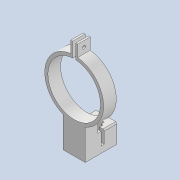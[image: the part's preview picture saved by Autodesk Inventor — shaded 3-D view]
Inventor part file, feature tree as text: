
AUTODESK INVENTOR PART (.ipt)
format: ipt  version: 2020 (Build 240168000, 168)  size: 200,704 bytes
history: native  units: mm
features: sketch x6, extrude x5, hole x1, chamfer x1, projected_geometry x1
ambient origin geometry x8: Origin, YZ Plane, XZ Plane, XY Plane, X Axis, Y Axis, Z Axis, Center Point
bodies: Solid1 (feature_tree)
feature tree (14):
  extrude  "Extrusion1"  Depth=93.0mm
  hole  "Hole1"  [1 undecoded]
  extrude  "Extrusion2"  Depth=3.0mm
  extrude  "Extrusion3"  Depth=50.0mm
  extrude  "Extrusion5"  Depth=30.0mm TaperAngle=0.0deg
  extrude  "Extrusion6"  Depth=30.0mm
  chamfer  "Chamfer1"  [1 undecoded]
  sketch  "Sketch1"  dims[d0=83.0mm d1=93.0mm]
  sketch  "Sketch2"  dims[d4=3.0mm d5=5.0mm]
  sketch  "Sketch3"  dims[d6=3.0mm d7=3.0mm]
  projected_geometry  "Projected Loop1"
  sketch  "Sketch4"  dims[d8=35.0mm d9=50.0mm]
  sketch  "Sketch6"  dims[d10=20.0mm d11=0.0mm]
  sketch  "Sketch9"  dims[d12=5.0mm d13=6.0mm d14=4.0mm d15=2.0mm d16=90.0deg d17=8.0mm d18=20.594885mm d19=30.0mm d20=0.0mm d22=30.0mm d23=0.0mm d24=0.0mm d28=0.25mm d29=0.0mm d30=0.0mm d31=5.0mm d32=20.0mm d33=28.0mm d34=0.0mm d35=15.275691mm d36=32.858366mm d37=2.0mm d38=2.0mm d39=45.0deg]
note: 2 required parameter values undecoded (feature->parameter linkage not recoverable at this tier; creation-order binding heuristic only, values carry confidence <= 0.55)
